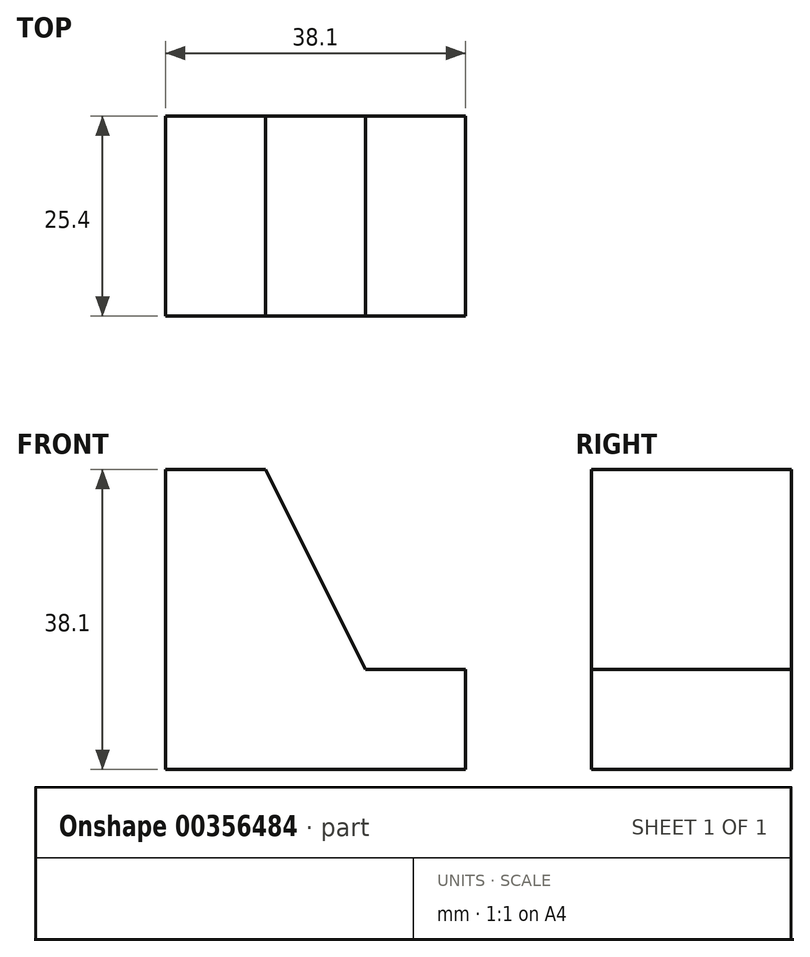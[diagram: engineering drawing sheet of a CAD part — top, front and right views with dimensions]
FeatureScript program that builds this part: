
annotation { "Feature Type Name" : "Feature", "Feature Type Description" : "" }
export const myFeature = defineFeature(function(context is Context, id is Id, definition is map)
    precondition{}
    {
        {
            var Q0;
            Q0=qCreatedBy(makeId("Front.planeOp"),FACE);
            var sketch = newSketch(context, id + "F0", { "sketchPlane" : qUnion([Q0])});
            skLineSegment(sketch, "E0", {"start": v(0, 0) * mm, "end": v(0, 38.1) * mm});
            skLineSegment(sketch, "E1", {"start": v(0, 38.1) * mm, "end": v(12.7, 38.1) * mm});
            skLineSegment(sketch, "E2", {"start": v(12.7, 38.1) * mm, "end": v(25.4, 12.7) * mm});
            skLineSegment(sketch, "E3", {"start": v(25.4, 12.7) * mm, "end": v(38.1, 12.7) * mm});
            skLineSegment(sketch, "E4", {"start": v(38.1, 12.7) * mm, "end": v(38.1, 0) * mm});
            skLineSegment(sketch, "E5", {"start": v(38.1, 0) * mm, "end": v(0, 0) * mm});
            skSolve(sketch);
        }
        {
            var Q0;
            Q0 = qSketchRegion(id + "F0", true);
            extrude(context, id + "F1", {"entities" : qUnion([Q0]), "depth" : 25.4 * mm});
        }
    });
